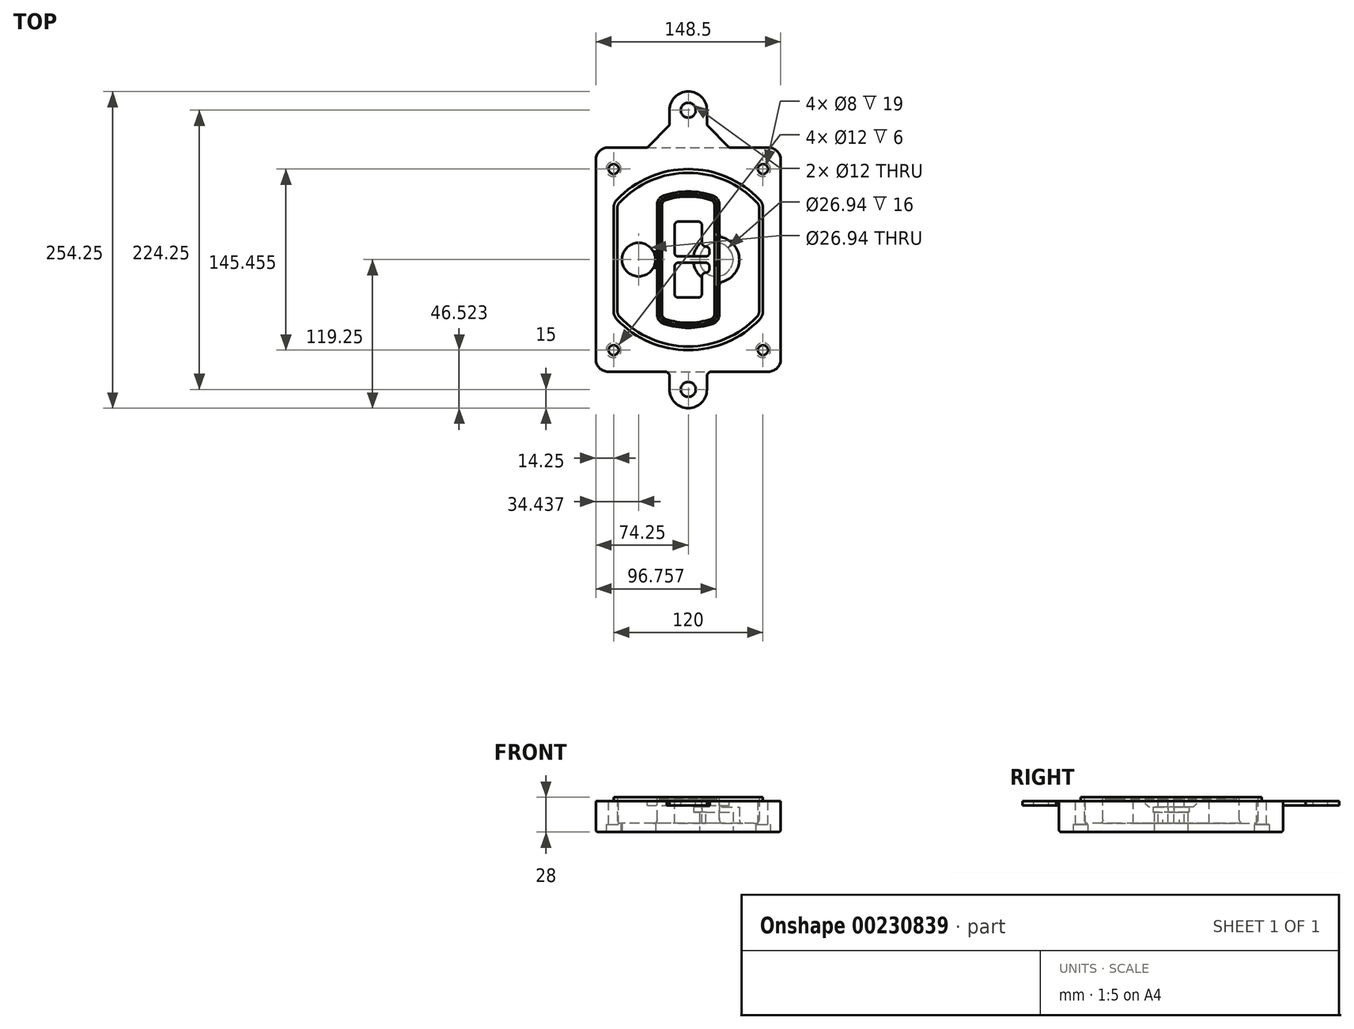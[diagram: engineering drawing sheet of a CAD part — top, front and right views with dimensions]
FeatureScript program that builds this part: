
annotation { "Feature Type Name" : "Feature", "Feature Type Description" : "" }
export const myFeature = defineFeature(function(context is Context, id is Id, definition is map)
    precondition{}
    {
        {
            var Q0;
            Q0=qCreatedBy(makeId("Top.planeOp"),FACE);
            var sketch = newSketch(context, id + "F0", { "sketchPlane" : qUnion([Q0])});
            skPoint(sketch, "E0.rect.middle", {"position": v(0, 0) * mm});
            skLineSegment(sketch, "E1.bottom", {"start": v(-64.25, -90) * mm, "end": v(64.25, -90) * mm});
            skLineSegment(sketch, "E1.top", {"start": v(-64.25, 90) * mm, "end": v(64.25, 90) * mm});
            skLineSegment(sketch, "E1.left", {"start": v(-74.25, -80) * mm, "end": v(-74.25, 80) * mm});
            skLineSegment(sketch, "E1.right", {"start": v(74.25, -80) * mm, "end": v(74.25, 80) * mm});
            skLineSegment(sketch, "E2", {"start": v(-74.25, 90) * mm, "end": v(74.25, -90) * mm, "construction": true});
            skLineSegment(sketch, "E3", {"start": v(74.25, 90) * mm, "end": v(-74.25, -90) * mm, "construction": true});
            skCircle(sketch, "E4", {"center": v(-60, 72.73) * mm, "radius": 4 * mm});
            skCircle(sketch, "E5", {"center": v(60, 72.73) * mm, "radius": 4 * mm});
            skCircle(sketch, "E6", {"center": v(60, -72.73) * mm, "radius": 4 * mm});
            skCircle(sketch, "E7", {"center": v(-60, -72.73) * mm, "radius": 4 * mm});
            skLineSegment(sketch, "E8", {"start": v(-60, 72.73) * mm, "end": v(60, 72.73) * mm, "construction": true});
            skLineSegment(sketch, "E9", {"start": v(60, 72.73) * mm, "end": v(60, -72.73) * mm, "construction": true});
            skLineSegment(sketch, "E10", {"start": v(60, -72.73) * mm, "end": v(-60, -72.73) * mm, "construction": true});
            skLineSegment(sketch, "E11", {"start": v(-60, -72.73) * mm, "end": v(-60, 72.73) * mm, "construction": true});
            skLineSegment(sketch, "E12", {"start": v(-60, 41.18) * mm, "end": v(-60, -41.18) * mm});
            skLineSegment(sketch, "E13", {"start": v(60, 41.18) * mm, "end": v(60, -41.18) * mm});
            skArc(sketch, "E14", {"start": v(57.27, 48.05) * mm, "mid": v(0, 72.73) * mm, "end": v(-57.27, 48.05) * mm});
            skArc(sketch, "E15", {"start": v(-57.27, -48.05) * mm, "mid": v(0, -72.73) * mm, "end": v(57.27, -48.05) * mm});
            skLineSegment(sketch, "E16", {"start": v(-60, 0) * mm, "end": v(60, 0) * mm, "construction": true});
            skPoint(sketch, "E17.visualSharp", {"position": v(-60, -45) * mm});
            skArc(sketch, "E17.filletArc", {"start": v(-60, -41.18) * mm, "mid": v(-59.3, -44.87) * mm, "end": v(-57.27, -48.05) * mm});
            skPoint(sketch, "E18.visualSharp", {"position": v(-60, 45) * mm});
            skArc(sketch, "E18.filletArc", {"start": v(-57.27, 48.05) * mm, "mid": v(-59.3, 44.87) * mm, "end": v(-60, 41.18) * mm});
            skPoint(sketch, "E19.visualSharp", {"position": v(60, 45) * mm});
            skArc(sketch, "E19.filletArc", {"start": v(60, 41.18) * mm, "mid": v(59.3, 44.87) * mm, "end": v(57.27, 48.05) * mm});
            skPoint(sketch, "E20.visualSharp", {"position": v(60, -45) * mm});
            skArc(sketch, "E20.filletArc", {"start": v(57.27, -48.05) * mm, "mid": v(59.3, -44.87) * mm, "end": v(60, -41.18) * mm});
            skPoint(sketch, "E21.visualSharp", {"position": v(-74.25, 90) * mm});
            skArc(sketch, "E21.filletArc", {"start": v(-64.25, 90) * mm, "mid": v(-71.32, 87.07) * mm, "end": v(-74.25, 80) * mm});
            skPoint(sketch, "E22.visualSharp", {"position": v(74.25, 90) * mm});
            skArc(sketch, "E22.filletArc", {"start": v(74.25, 80) * mm, "mid": v(71.32, 87.07) * mm, "end": v(64.25, 90) * mm});
            skPoint(sketch, "E23.visualSharp", {"position": v(74.25, -90) * mm});
            skArc(sketch, "E23.filletArc", {"start": v(64.25, -90) * mm, "mid": v(71.32, -87.07) * mm, "end": v(74.25, -80) * mm});
            skPoint(sketch, "E24.visualSharp", {"position": v(-74.25, -90) * mm});
            skArc(sketch, "E24.filletArc", {"start": v(-74.25, -80) * mm, "mid": v(-71.32, -87.07) * mm, "end": v(-64.25, -90) * mm});
            skArc(sketch, "E25.0", {"start": v(57, 41.18) * mm, "mid": v(56.5, 43.76) * mm, "end": v(55.09, 45.99) * mm});
            skLineSegment(sketch, "E25.1", {"start": v(57, 41.18) * mm, "end": v(57, -41.18) * mm});
            skArc(sketch, "E25.2", {"start": v(55.09, -45.99) * mm, "mid": v(56.5, -43.76) * mm, "end": v(57, -41.18) * mm});
            skArc(sketch, "E25.3", {"start": v(-55.09, -45.99) * mm, "mid": v(0, -69.73) * mm, "end": v(55.09, -45.99) * mm});
            skArc(sketch, "E25.4", {"start": v(-57, -41.18) * mm, "mid": v(-56.5, -43.76) * mm, "end": v(-55.09, -45.99) * mm});
            skArc(sketch, "E25.5", {"start": v(55.09, 45.99) * mm, "mid": v(0, 69.73) * mm, "end": v(-55.09, 45.99) * mm});
            skLineSegment(sketch, "E25.6", {"start": v(-57, 41.18) * mm, "end": v(-57, -41.18) * mm});
            skArc(sketch, "E25.7", {"start": v(-55.09, 45.99) * mm, "mid": v(-56.5, 43.76) * mm, "end": v(-57, 41.18) * mm});
            skArc(sketch, "E26.0", {"start": v(-60.18, 50.8) * mm, "mid": v(-63, 46.35) * mm, "end": v(-64, 41.18) * mm});
            skArc(sketch, "E26.1", {"start": v(60.18, 50.8) * mm, "mid": v(0, 76.73) * mm, "end": v(-60.18, 50.8) * mm});
            skArc(sketch, "E26.2", {"start": v(64, 41.18) * mm, "mid": v(63, 46.35) * mm, "end": v(60.18, 50.8) * mm});
            skLineSegment(sketch, "E26.3", {"start": v(64, 41.18) * mm, "end": v(64, -41.18) * mm});
            skArc(sketch, "E26.4", {"start": v(60.18, -50.8) * mm, "mid": v(63, -46.35) * mm, "end": v(64, -41.18) * mm});
            skLineSegment(sketch, "E26.5", {"start": v(-64, 41.18) * mm, "end": v(-64, -41.18) * mm});
            skArc(sketch, "E26.6", {"start": v(-60.18, -50.8) * mm, "mid": v(0, -76.73) * mm, "end": v(60.18, -50.8) * mm});
            skArc(sketch, "E26.7", {"start": v(-64, -41.18) * mm, "mid": v(-63, -46.35) * mm, "end": v(-60.18, -50.8) * mm});
            skSolve(sketch);
        }
        {
            var Q0;
            Q0=makeQuery(id+"F0.imprint","IMPRINT",FACE,{"disambiguationData":[TD([[makeQuery(id+"F0.imprint","IMPRINT",EDGE,{"derivedFrom":sQuery(id+"F0.wireOp",EDGE,"E1.bottom")}),1.0]])]});
            var Q1;
            Q1=makeQuery(id+"F0.imprint","IMPRINT",FACE,{"disambiguationData":[TD([[makeQuery(id+"F0.imprint","IMPRINT",EDGE,{"derivedFrom":sQuery(id+"F0.wireOp",EDGE,"E12")}),1.0]])]});
            var Q2;
            Q2=makeQuery(id+"F0.imprint","IMPRINT",FACE,{"disambiguationData":[TD([[makeQuery(id+"F0.imprint","IMPRINT",EDGE,{"derivedFrom":sQuery(id+"F0.wireOp",EDGE,"E25.0")}),1.0]])]});
            var Q3;
            Q3=makeQuery(id+"F0.imprint","IMPRINT",FACE,{"disambiguationData":[TD([[makeQuery(id+"F0.imprint","IMPRINT",EDGE,{"derivedFrom":sQuery(id+"F0.wireOp",EDGE,"E12")}),-1.0]])]});
            extrude(context, id + "F1", {"entities" : qUnion([Q0, Q1, Q2, Q3]), "oppositeDirection" : true, "depth" : 25 * mm});
        }
        {
            var Q0;
            Q0=makeQuery(id+"F0.imprint","IMPRINT",FACE,{"disambiguationData":[TD([[makeQuery(id+"F0.imprint","IMPRINT",EDGE,{"derivedFrom":sQuery(id+"F0.wireOp",EDGE,"E12")}),1.0]])]});
            extrude(context, id + "F2", {"entities" : qUnion([Q0]), "operationType" : NewBodyOperationType.ADD, "depth" : 3 * mm});
        }
        {
            var Q0;
            Q0=makeQuery(id+"F0.imprint","IMPRINT",FACE,{"disambiguationData":[TD([[makeQuery(id+"F0.imprint","IMPRINT",EDGE,{"derivedFrom":sQuery(id+"F0.wireOp",EDGE,"E25.0")}),1.0]])]});
            extrude(context, id + "F3", {"entities" : qUnion([Q0]), "operationType" : NewBodyOperationType.REMOVE, "oppositeDirection" : true, "depth" : 18 * mm});
        }
        {
            var Q0;
            Q0=makeQuery(id+"F2.opExtrude","CAP_FACE",FACE,{"disambiguationData":[OSD([sQuery(id+"F0.wireOp",EDGE,"E12"),sQuery(id+"F0.wireOp",EDGE,"E13"),sQuery(id+"F0.wireOp",EDGE,"E14"),sQuery(id+"F0.wireOp",EDGE,"E15"),sQuery(id+"F0.wireOp",EDGE,"E17.filletArc"),sQuery(id+"F0.wireOp",EDGE,"E18.filletArc"),sQuery(id+"F0.wireOp",EDGE,"E19.filletArc"),sQuery(id+"F0.wireOp",EDGE,"E20.filletArc"),sQuery(id+"F0.wireOp",EDGE,"E25.0"),sQuery(id+"F0.wireOp",EDGE,"E25.1"),sQuery(id+"F0.wireOp",EDGE,"E25.2"),sQuery(id+"F0.wireOp",EDGE,"E25.3"),sQuery(id+"F0.wireOp",EDGE,"E25.4"),sQuery(id+"F0.wireOp",EDGE,"E25.5"),sQuery(id+"F0.wireOp",EDGE,"E25.6"),sQuery(id+"F0.wireOp",EDGE,"E25.7")])],"isStart":false});
            var sketch = newSketch(context, id + "F4", { "sketchPlane" : qUnion([Q0])});
            skArc(sketch, "E27.0", {"start": v(-19.58, -51.49) * mm, "mid": v(0, -54.73) * mm, "end": v(19.58, -51.49) * mm});
            skArc(sketch, "E28.0", {"start": v(19.58, 51.49) * mm, "mid": v(0, 54.73) * mm, "end": v(-19.58, 51.49) * mm});
            skLineSegment(sketch, "E29", {"start": v(-25, 43.91) * mm, "end": v(-25, -43.91) * mm});
            skLineSegment(sketch, "E30", {"start": v(25, 43.91) * mm, "end": v(25, -43.91) * mm});
            skLineSegment(sketch, "E31", {"start": v(-25, 49.35) * mm, "end": v(25, 49.35) * mm, "construction": true});
            skLineSegment(sketch, "E32", {"start": v(-25, -49.35) * mm, "end": v(25, -49.35) * mm, "construction": true});
            skPoint(sketch, "E33.visualSharp", {"position": v(-25, 49.35) * mm});
            skArc(sketch, "E33.filletArc", {"start": v(-19.58, 51.49) * mm, "mid": v(-23.5, 48.57) * mm, "end": v(-25, 43.91) * mm});
            skPoint(sketch, "E34.visualSharp", {"position": v(25, 49.35) * mm});
            skArc(sketch, "E34.filletArc", {"start": v(25, 43.91) * mm, "mid": v(23.5, 48.57) * mm, "end": v(19.58, 51.49) * mm});
            skPoint(sketch, "E35.visualSharp", {"position": v(25, -49.35) * mm});
            skArc(sketch, "E35.filletArc", {"start": v(19.58, -51.49) * mm, "mid": v(23.5, -48.57) * mm, "end": v(25, -43.91) * mm});
            skPoint(sketch, "E36.visualSharp", {"position": v(-25, -49.35) * mm});
            skArc(sketch, "E36.filletArc", {"start": v(-25, -43.91) * mm, "mid": v(-23.5, -48.57) * mm, "end": v(-19.58, -51.49) * mm});
            skArc(sketch, "E37.0", {"start": v(55.09, 45.99) * mm, "mid": v(0, 69.73) * mm, "end": v(-55.09, 45.99) * mm});
            skArc(sketch, "E37.1", {"start": v(-55.09, 45.99) * mm, "mid": v(-56.5, 43.76) * mm, "end": v(-57, 41.18) * mm});
            skLineSegment(sketch, "E37.2", {"start": v(-57, 41.18) * mm, "end": v(-57, -41.18) * mm});
            skArc(sketch, "E37.3", {"start": v(-57, -41.18) * mm, "mid": v(-56.5, -43.76) * mm, "end": v(-55.09, -45.99) * mm});
            skArc(sketch, "E37.4", {"start": v(-55.09, -45.99) * mm, "mid": v(0, -69.73) * mm, "end": v(55.09, -45.99) * mm});
            skArc(sketch, "E37.5", {"start": v(55.09, -45.99) * mm, "mid": v(56.5, -43.76) * mm, "end": v(57, -41.18) * mm});
            skLineSegment(sketch, "E37.6", {"start": v(57, 41.18) * mm, "end": v(57, -41.18) * mm});
            skArc(sketch, "E37.7", {"start": v(57, 41.18) * mm, "mid": v(56.5, 43.76) * mm, "end": v(55.09, 45.99) * mm});
            skLineSegment(sketch, "E38.0", {"start": v(23, 43.91) * mm, "end": v(23, -43.91) * mm});
            skArc(sketch, "E38.1", {"start": v(18.93, -49.6) * mm, "mid": v(21.88, -47.4) * mm, "end": v(23, -43.91) * mm});
            skArc(sketch, "E38.2", {"start": v(-18.93, -49.6) * mm, "mid": v(0, -52.73) * mm, "end": v(18.93, -49.6) * mm});
            skArc(sketch, "E38.3", {"start": v(-23, -43.91) * mm, "mid": v(-21.88, -47.4) * mm, "end": v(-18.93, -49.6) * mm});
            skLineSegment(sketch, "E38.4", {"start": v(-23, 43.91) * mm, "end": v(-23, -43.91) * mm});
            skArc(sketch, "E38.5", {"start": v(23, 43.91) * mm, "mid": v(21.88, 47.4) * mm, "end": v(18.93, 49.6) * mm});
            skArc(sketch, "E38.6", {"start": v(-18.93, 49.6) * mm, "mid": v(-21.88, 47.4) * mm, "end": v(-23, 43.91) * mm});
            skArc(sketch, "E38.7", {"start": v(18.93, 49.6) * mm, "mid": v(0, 52.73) * mm, "end": v(-18.93, 49.6) * mm});
            skArc(sketch, "E39.0", {"start": v(21, 43.91) * mm, "mid": v(20.25, 46.24) * mm, "end": v(18.29, 47.7) * mm});
            skLineSegment(sketch, "E39.1", {"start": v(21, 43.91) * mm, "end": v(21, -43.91) * mm});
            skArc(sketch, "E39.2", {"start": v(18.29, -47.7) * mm, "mid": v(20.25, -46.24) * mm, "end": v(21, -43.91) * mm});
            skArc(sketch, "E39.3", {"start": v(-18.29, -47.7) * mm, "mid": v(0, -50.73) * mm, "end": v(18.29, -47.7) * mm});
            skArc(sketch, "E39.4", {"start": v(-21, -43.91) * mm, "mid": v(-20.25, -46.24) * mm, "end": v(-18.29, -47.7) * mm});
            skArc(sketch, "E39.5", {"start": v(18.29, 47.7) * mm, "mid": v(0, 50.73) * mm, "end": v(-18.29, 47.7) * mm});
            skLineSegment(sketch, "E39.6", {"start": v(-21, 43.91) * mm, "end": v(-21, -43.91) * mm});
            skArc(sketch, "E39.7", {"start": v(-18.29, 47.7) * mm, "mid": v(-20.25, 46.24) * mm, "end": v(-21, 43.91) * mm});
            skLineSegment(sketch, "E40", {"start": v(-25, 0) * mm, "end": v(25, 0) * mm, "construction": true});
            skLineSegment(sketch, "E41", {"start": v(-11, 5.5) * mm, "end": v(-11, 27.5) * mm});
            skLineSegment(sketch, "E42", {"start": v(-8, 30.5) * mm, "end": v(8, 30.5) * mm});
            skLineSegment(sketch, "E43", {"start": v(11, 27.5) * mm, "end": v(11, 13.5) * mm});
            skLineSegment(sketch, "E44", {"start": v(14, 10.5) * mm, "end": v(14, 10.5) * mm});
            skLineSegment(sketch, "E45", {"start": v(17, 7.5) * mm, "end": v(17, 5.5) * mm});
            skLineSegment(sketch, "E46", {"start": v(14, 2.5) * mm, "end": v(-8, 2.5) * mm});
            skPoint(sketch, "E47.visualSharp", {"position": v(-11, 30.5) * mm});
            skArc(sketch, "E47.filletArc", {"start": v(-8, 30.5) * mm, "mid": v(-10.12, 29.62) * mm, "end": v(-11, 27.5) * mm});
            skPoint(sketch, "E48.visualSharp", {"position": v(11, 30.5) * mm});
            skArc(sketch, "E48.filletArc", {"start": v(11, 27.5) * mm, "mid": v(10.12, 29.62) * mm, "end": v(8, 30.5) * mm});
            skPoint(sketch, "E49.visualSharp", {"position": v(11, 10.5) * mm});
            skArc(sketch, "E49.filletArc", {"start": v(11, 13.5) * mm, "mid": v(11.88, 11.38) * mm, "end": v(14, 10.5) * mm});
            skPoint(sketch, "E50.visualSharp", {"position": v(17, 10.5) * mm});
            skArc(sketch, "E50.filletArc", {"start": v(17, 7.5) * mm, "mid": v(16.12, 9.62) * mm, "end": v(14, 10.5) * mm});
            skPoint(sketch, "E51.visualSharp", {"position": v(17, 2.5) * mm});
            skArc(sketch, "E51.filletArc", {"start": v(14, 2.5) * mm, "mid": v(16.12, 3.38) * mm, "end": v(17, 5.5) * mm});
            skPoint(sketch, "E52.visualSharp", {"position": v(-11, 2.5) * mm});
            skArc(sketch, "E52.filletArc", {"start": v(-11, 5.5) * mm, "mid": v(-10.12, 3.38) * mm, "end": v(-8, 2.5) * mm});
            skLineSegment(sketch, "E53.0.MirrorCS", {"start": v(14, -2.5) * mm, "end": v(-8, -2.5) * mm});
            skArc(sketch, "E54.0.MirrorCS", {"start": v(-11, -5.5) * mm, "mid": v(-10.12, -3.38) * mm, "end": v(-8, -2.5) * mm});
            skLineSegment(sketch, "E55.0.MirrorCS", {"start": v(-11, -5.5) * mm, "end": v(-11, -27.5) * mm});
            skArc(sketch, "E56.0.MirrorCS", {"start": v(-8, -30.5) * mm, "mid": v(-10.12, -29.62) * mm, "end": v(-11, -27.5) * mm});
            skLineSegment(sketch, "E57.0.MirrorCS", {"start": v(-8, -30.5) * mm, "end": v(8, -30.5) * mm});
            skArc(sketch, "E58.0.MirrorCS", {"start": v(11, -27.5) * mm, "mid": v(10.12, -29.62) * mm, "end": v(8, -30.5) * mm});
            skLineSegment(sketch, "E59.0.MirrorCS", {"start": v(11, -27.5) * mm, "end": v(11, -13.5) * mm});
            skArc(sketch, "E60.0.MirrorCS", {"start": v(11, -13.5) * mm, "mid": v(11.88, -11.38) * mm, "end": v(14, -10.5) * mm});
            skArc(sketch, "E61.0.MirrorCS", {"start": v(17, -7.5) * mm, "mid": v(16.12, -9.62) * mm, "end": v(14, -10.5) * mm});
            skLineSegment(sketch, "E62.0.MirrorCS", {"start": v(17, -7.5) * mm, "end": v(17, -5.5) * mm});
            skArc(sketch, "E63.0.MirrorCS", {"start": v(14, -2.5) * mm, "mid": v(16.12, -3.38) * mm, "end": v(17, -5.5) * mm});
            skSolve(sketch);
        }
        {
            var Q0;
            Q0=makeQuery(id+"F4.imprint","IMPRINT",FACE,{"disambiguationData":[TD([[makeQuery(id+"F4.imprint","IMPRINT",EDGE,{"derivedFrom":sQuery(id+"F4.wireOp",EDGE,"E27.0")}),1.0]])]});
            var Q1;
            Q1=makeQuery(id+"F4.imprint","IMPRINT",FACE,{"disambiguationData":[TD([[makeQuery(id+"F4.imprint","IMPRINT",EDGE,{"derivedFrom":sQuery(id+"F4.wireOp",EDGE,"E38.0")}),-1.0]])]});
            var Q2;
            Q2=makeQuery(id+"F4.imprint","IMPRINT",FACE,{"disambiguationData":[TD([[makeQuery(id+"F4.imprint","IMPRINT",EDGE,{"derivedFrom":sQuery(id+"F4.wireOp",EDGE,"E39.0")}),1.0]])]});
            extrude(context, id + "F5", {"entities" : qUnion([Q0, Q1, Q2]), "operationType" : NewBodyOperationType.ADD, "endBound" : BoundingType.UP_TO_NEXT, "oppositeDirection" : true, "depth" : 25 * mm});
        }
        {
            var Q0;
            Q0=makeQuery(id+"F4.imprint","IMPRINT",FACE,{"disambiguationData":[TD([[makeQuery(id+"F4.imprint","IMPRINT",EDGE,{"derivedFrom":sQuery(id+"F4.wireOp",EDGE,"E38.0")}),-1.0]])]});
            extrude(context, id + "F6", {"entities" : qUnion([Q0]), "operationType" : NewBodyOperationType.REMOVE, "oppositeDirection" : true, "depth" : 2 * mm});
        }
        {
            var Q0;
            Q0=makeQuery(id+"F1.opExtrude","CAP_FACE",FACE,{"disambiguationData":[OSD([sQuery(id+"F0.wireOp",EDGE,"E1.bottom"),sQuery(id+"F0.wireOp",EDGE,"E1.top"),sQuery(id+"F0.wireOp",EDGE,"E1.left"),sQuery(id+"F0.wireOp",EDGE,"E1.right"),sQuery(id+"F0.wireOp",EDGE,"E4"),sQuery(id+"F0.wireOp",EDGE,"E5"),sQuery(id+"F0.wireOp",EDGE,"E6"),sQuery(id+"F0.wireOp",EDGE,"E7"),sQuery(id+"F0.wireOp",EDGE,"E21.filletArc"),sQuery(id+"F0.wireOp",EDGE,"E22.filletArc"),sQuery(id+"F0.wireOp",EDGE,"E23.filletArc"),sQuery(id+"F0.wireOp",EDGE,"E24.filletArc")])],"isStart":false});
            var sketch = newSketch(context, id + "F7", { "sketchPlane" : qUnion([Q0])});
            skCircle(sketch, "E64", {"center": v(22.5, 0) * mm, "radius": 13.47 * mm});
            skCircle(sketch, "E65", {"center": v(-39.81, 0) * mm, "radius": 13.47 * mm});
            skLineSegment(sketch, "E66", {"start": v(74.25, 0) * mm, "end": v(-74.25, 0) * mm});
            skCircle(sketch, "E67", {"center": v(22.5, 0) * mm, "radius": 18.47 * mm});
            skCircle(sketch, "E68", {"center": v(60, -72.73) * mm, "radius": 6 * mm});
            skCircle(sketch, "E69", {"center": v(-60, -72.73) * mm, "radius": 6 * mm});
            skCircle(sketch, "E70", {"center": v(-60, 72.73) * mm, "radius": 6 * mm});
            skCircle(sketch, "E71", {"center": v(60, 72.73) * mm, "radius": 6 * mm});
            skSolve(sketch);
        }
        {
            var Q0;
            {var subQ1=sQuery(id+"F7.wireOp",EDGE,"E66");var subQ4=sQuery(id+"F7.wireOp",EDGE,"E64");var subQ6=makeQuery(id+"F7.imprint","INTERSECT",VERTEX,{"disambiguationData":[OD(0.0)],"derivedFrom":[subQ4,subQ1]});Q0=makeQuery(id+"F7.imprint","IMPRINT",FACE,{"disambiguationData":[TD([[makeQuery(id+"F7.imprint","IMPRINT",EDGE,{"disambiguationData":[TD([[subQ6,-1.0]])],"derivedFrom":subQ4}),-1.0]])]});}
            var Q1;
            {var subQ0=sQuery(id+"F7.wireOp",EDGE,"E66");var subQ1=sQuery(id+"F7.wireOp",EDGE,"E64");var subQ3=makeQuery(id+"F7.imprint","INTERSECT",VERTEX,{"disambiguationData":[OD(0.0)],"derivedFrom":[subQ1,subQ0]});Q1=makeQuery(id+"F7.imprint","IMPRINT",FACE,{"disambiguationData":[TD([[makeQuery(id+"F7.imprint","IMPRINT",EDGE,{"disambiguationData":[TD([[subQ3,-1.0]])],"derivedFrom":subQ1}),1.0]])]});}
            var Q2;
            {var subQ0=sQuery(id+"F7.wireOp",EDGE,"E66");var subQ1=sQuery(id+"F7.wireOp",EDGE,"E64");var subQ3=makeQuery(id+"F7.imprint","INTERSECT",VERTEX,{"disambiguationData":[OD(0.0)],"derivedFrom":[subQ1,subQ0]});Q2=makeQuery(id+"F7.imprint","IMPRINT",FACE,{"disambiguationData":[TD([[makeQuery(id+"F7.imprint","IMPRINT",EDGE,{"disambiguationData":[TD([[subQ3,1.0]])],"derivedFrom":subQ1}),1.0]])]});}
            var Q3;
            {var subQ1=sQuery(id+"F7.wireOp",EDGE,"E66");var subQ4=sQuery(id+"F7.wireOp",EDGE,"E64");var subQ6=makeQuery(id+"F7.imprint","INTERSECT",VERTEX,{"disambiguationData":[OD(0.0)],"derivedFrom":[subQ4,subQ1]});Q3=makeQuery(id+"F7.imprint","IMPRINT",FACE,{"disambiguationData":[TD([[makeQuery(id+"F7.imprint","IMPRINT",EDGE,{"disambiguationData":[TD([[subQ6,1.0]])],"derivedFrom":subQ4}),-1.0]])]});}
            extrude(context, id + "F8", {"entities" : qUnion([Q0, Q1, Q2, Q3]), "operationType" : NewBodyOperationType.ADD, "oppositeDirection" : true, "depth" : 20 * mm});
        }
        {
            var Q0;
            {var subQ0=sQuery(id+"F7.wireOp",EDGE,"E66");var subQ1=sQuery(id+"F7.wireOp",EDGE,"E64");var subQ3=makeQuery(id+"F7.imprint","INTERSECT",VERTEX,{"disambiguationData":[OD(0.0)],"derivedFrom":[subQ1,subQ0]});Q0=makeQuery(id+"F7.imprint","IMPRINT",FACE,{"disambiguationData":[TD([[makeQuery(id+"F7.imprint","IMPRINT",EDGE,{"disambiguationData":[TD([[subQ3,-1.0]])],"derivedFrom":subQ1}),1.0]])]});}
            var Q1;
            {var subQ0=sQuery(id+"F7.wireOp",EDGE,"E66");var subQ1=sQuery(id+"F7.wireOp",EDGE,"E64");var subQ3=makeQuery(id+"F7.imprint","INTERSECT",VERTEX,{"disambiguationData":[OD(0.0)],"derivedFrom":[subQ1,subQ0]});Q1=makeQuery(id+"F7.imprint","IMPRINT",FACE,{"disambiguationData":[TD([[makeQuery(id+"F7.imprint","IMPRINT",EDGE,{"disambiguationData":[TD([[subQ3,1.0]])],"derivedFrom":subQ1}),1.0]])]});}
            extrude(context, id + "F9", {"entities" : qUnion([Q0, Q1]), "operationType" : NewBodyOperationType.REMOVE, "oppositeDirection" : true, "depth" : 16 * mm});
        }
        {
            var Q0;
            {var subQ0=sQuery(id+"F7.wireOp",EDGE,"E66");var subQ1=sQuery(id+"F7.wireOp",EDGE,"E65");var subQ3=makeQuery(id+"F7.imprint","INTERSECT",VERTEX,{"disambiguationData":[OD(0.0)],"derivedFrom":[subQ1,subQ0]});Q0=makeQuery(id+"F7.imprint","IMPRINT",FACE,{"disambiguationData":[TD([[makeQuery(id+"F7.imprint","IMPRINT",EDGE,{"disambiguationData":[TD([[subQ3,-1.0]])],"derivedFrom":subQ1}),1.0]])]});}
            var Q1;
            {var subQ0=sQuery(id+"F7.wireOp",EDGE,"E66");var subQ1=sQuery(id+"F7.wireOp",EDGE,"E65");var subQ3=makeQuery(id+"F7.imprint","INTERSECT",VERTEX,{"disambiguationData":[OD(0.0)],"derivedFrom":[subQ1,subQ0]});Q1=makeQuery(id+"F7.imprint","IMPRINT",FACE,{"disambiguationData":[TD([[makeQuery(id+"F7.imprint","IMPRINT",EDGE,{"disambiguationData":[TD([[subQ3,1.0]])],"derivedFrom":subQ1}),1.0]])]});}
            extrude(context, id + "F10", {"entities" : qUnion([Q0, Q1]), "operationType" : NewBodyOperationType.REMOVE, "oppositeDirection" : true, "depth" : 25 * mm});
        }
        {
            var Q0;
            Q0=makeQuery(id+"F7.imprint","IMPRINT",FACE,{"disambiguationData":[TD([[makeQuery(id+"F7.imprint","IMPRINT",EDGE,{"derivedFrom":sQuery(id+"F7.wireOp",EDGE,"E68")}),1.0]])]});
            var Q1;
            Q1=makeQuery(id+"F7.imprint","IMPRINT",FACE,{"disambiguationData":[TD([[makeQuery(id+"F7.imprint","IMPRINT",EDGE,{"derivedFrom":makeQuery(id+"F1.opExtrude","CAP_EDGE",EDGE,{"disambiguationData":[OSD([sQuery(id+"F0.wireOp",EDGE,"E5")])],"isStart":false})}),-1.0]])]});
            var Q2;
            Q2=makeQuery(id+"F7.imprint","IMPRINT",FACE,{"disambiguationData":[TD([[makeQuery(id+"F7.imprint","IMPRINT",EDGE,{"derivedFrom":sQuery(id+"F7.wireOp",EDGE,"E69")}),1.0]])]});
            var Q3;
            Q3=makeQuery(id+"F7.imprint","IMPRINT",FACE,{"disambiguationData":[TD([[makeQuery(id+"F7.imprint","IMPRINT",EDGE,{"derivedFrom":makeQuery(id+"F1.opExtrude","CAP_EDGE",EDGE,{"disambiguationData":[OSD([sQuery(id+"F0.wireOp",EDGE,"E4")])],"isStart":false})}),-1.0]])]});
            var Q4;
            Q4=makeQuery(id+"F7.imprint","IMPRINT",FACE,{"disambiguationData":[TD([[makeQuery(id+"F7.imprint","IMPRINT",EDGE,{"derivedFrom":sQuery(id+"F7.wireOp",EDGE,"E70")}),1.0]])]});
            var Q5;
            Q5=makeQuery(id+"F7.imprint","IMPRINT",FACE,{"disambiguationData":[TD([[makeQuery(id+"F7.imprint","IMPRINT",EDGE,{"derivedFrom":makeQuery(id+"F1.opExtrude","CAP_EDGE",EDGE,{"disambiguationData":[OSD([sQuery(id+"F0.wireOp",EDGE,"E7")])],"isStart":false})}),-1.0]])]});
            var Q6;
            Q6=makeQuery(id+"F7.imprint","IMPRINT",FACE,{"disambiguationData":[TD([[makeQuery(id+"F7.imprint","IMPRINT",EDGE,{"derivedFrom":sQuery(id+"F7.wireOp",EDGE,"E71")}),1.0]])]});
            var Q7;
            Q7=makeQuery(id+"F7.imprint","IMPRINT",FACE,{"disambiguationData":[TD([[makeQuery(id+"F7.imprint","IMPRINT",EDGE,{"derivedFrom":makeQuery(id+"F1.opExtrude","CAP_EDGE",EDGE,{"disambiguationData":[OSD([sQuery(id+"F0.wireOp",EDGE,"E6")])],"isStart":false})}),-1.0]])]});
            extrude(context, id + "F11", {"entities" : qUnion([Q0, Q1, Q2, Q3, Q4, Q5, Q6, Q7]), "operationType" : NewBodyOperationType.REMOVE, "oppositeDirection" : true, "depth" : 6 * mm});
        }
        {
            var Q0;
            Q0=makeQuery(id+"F9.boolean.opBoolean","COPY",FACE,{"derivedFrom":makeQuery(id+"F9.opExtrude","CAP_FACE",FACE,{"disambiguationData":[OSD([sQuery(id+"F7.wireOp",EDGE,"E64")])],"isStart":false})});
            var sketch = newSketch(context, id + "F12", { "sketchPlane" : qUnion([Q0])});
            skArc(sketch, "E72.0", {"start": v(11, 14.45) * mm, "mid": v(6.45, 9.13) * mm, "end": v(4.2, 2.5) * mm});
            skArc(sketch, "E72.1", {"start": v(4.2, -2.5) * mm, "mid": v(6.45, -9.13) * mm, "end": v(11, -14.45) * mm});
            skLineSegment(sketch, "E73", {"start": v(4.2, -2.5) * mm, "end": v(14, -2.5) * mm});
            skLineSegment(sketch, "E74.0", {"start": v(14, 2.5) * mm, "end": v(4.2, 2.5) * mm});
            skArc(sketch, "E74.1", {"start": v(14, 2.5) * mm, "mid": v(16.12, 3.38) * mm, "end": v(17, 5.5) * mm});
            skLineSegment(sketch, "E74.2", {"start": v(17, 7.5) * mm, "end": v(17, 5.5) * mm});
            skArc(sketch, "E74.3", {"start": v(17, 7.5) * mm, "mid": v(16.12, 9.62) * mm, "end": v(14, 10.5) * mm});
            skArc(sketch, "E74.4", {"start": v(11, 13.5) * mm, "mid": v(11.88, 11.38) * mm, "end": v(14, 10.5) * mm});
            skLineSegment(sketch, "E74.5", {"start": v(11, 14.45) * mm, "end": v(11, 13.5) * mm});
            skLineSegment(sketch, "E74.7", {"start": v(14, -2.5) * mm, "end": v(4.2, -2.5) * mm});
            skArc(sketch, "E74.8", {"start": v(14, -2.5) * mm, "mid": v(16.12, -3.38) * mm, "end": v(17, -5.5) * mm});
            skLineSegment(sketch, "E74.9", {"start": v(17, -7.5) * mm, "end": v(17, -5.5) * mm});
            skArc(sketch, "E74.10", {"start": v(17, -7.5) * mm, "mid": v(16.12, -9.62) * mm, "end": v(14, -10.5) * mm});
            skArc(sketch, "E74.11", {"start": v(11, -13.5) * mm, "mid": v(11.88, -11.38) * mm, "end": v(14, -10.5) * mm});
            skLineSegment(sketch, "E74.12", {"start": v(11, -14.45) * mm, "end": v(11, -13.5) * mm});
            skPoint(sketch, "E75.orphan", {"position": v(11, -27.5) * mm});
            skPoint(sketch, "E76.orphan", {"position": v(-8, -2.5) * mm});
            skPoint(sketch, "E77.orphan", {"position": v(-8, 2.5) * mm});
            skPoint(sketch, "E78.orphan", {"position": v(11, 27.5) * mm});
            skSolve(sketch);
        }
        {
            var Q0;
            {var subQ7=sQuery(id+"F12.wireOp",EDGE,"E72.0");var subQ14=sQuery(id+"F12.wireOp",EDGE,"E72.1");var subQ16=sQuery(id+"F12.wireOp",EDGE,"E74.1");var subQ18=sQuery(id+"F12.wireOp",EDGE,"E74.8");Q0=qUnion([makeQuery(id+"F12.imprint","IMPRINT",FACE,{"disambiguationData":[TD([[makeQuery(id+"F12.imprint","IMPRINT",EDGE,{"derivedFrom":subQ7}),1.0]])]}),makeQuery(id+"F12.imprint","IMPRINT",FACE,{"disambiguationData":[TD([[makeQuery(id+"F12.imprint","IMPRINT",EDGE,{"derivedFrom":subQ14}),1.0]])]}),makeQuery(id+"F12.imprint","IMPRINT",FACE,{"disambiguationData":[TD([[makeQuery(id+"F12.imprint","IMPRINT",EDGE,{"derivedFrom":subQ16}),1.0]])]}),makeQuery(id+"F12.imprint","IMPRINT",FACE,{"disambiguationData":[TD([[makeQuery(id+"F12.imprint","IMPRINT",EDGE,{"derivedFrom":subQ18}),-1.0]])]})]);}
            var Q1;
            Q1=makeQuery(id+"F5.boolean.opBoolean","SPLIT",FACE,{"disambiguationData":[TD([makeQuery(id+"F5.opExtrude","SWEPT_FACE",FACE,{"disambiguationData":[OSD([sQuery(id+"F4.wireOp",EDGE,"E41")])]})])],"derivedFrom":makeQuery(id+"F3.boolean.opBoolean","COPY",FACE,{"derivedFrom":makeQuery(id+"F3.opExtrude","CAP_FACE",FACE,{"disambiguationData":[OSD([sQuery(id+"F0.wireOp",EDGE,"E25.0"),sQuery(id+"F0.wireOp",EDGE,"E25.1"),sQuery(id+"F0.wireOp",EDGE,"E25.2"),sQuery(id+"F0.wireOp",EDGE,"E25.3"),sQuery(id+"F0.wireOp",EDGE,"E25.4"),sQuery(id+"F0.wireOp",EDGE,"E25.5"),sQuery(id+"F0.wireOp",EDGE,"E25.6"),sQuery(id+"F0.wireOp",EDGE,"E25.7")])],"isStart":false})})});
            extrude(context, id + "F13", {"entities" : qUnion([Q0]), "operationType" : NewBodyOperationType.REMOVE, "endBound" : BoundingType.UP_TO_SURFACE, "endBoundEntityFace" : qUnion([Q1]), "depth" : 25 * mm});
        }
        {
            var Q0;
            Q0=makeQuery(id+"F3.boolean.opBoolean","COPY",EDGE,{"derivedFrom":makeQuery(id+"F3.opExtrude","CAP_EDGE",EDGE,{"disambiguationData":[OSD([sQuery(id+"F0.wireOp",EDGE,"E25.6")])],"isStart":false})});
            var Q1;
            Q1=makeQuery(id+"F8.boolean.opBoolean","INTERSECT",EDGE,{"derivedFrom":[makeQuery(id+"F5.opExtrude","SWEPT_FACE",FACE,{"disambiguationData":[OSD([sQuery(id+"F4.wireOp",EDGE,"E30")])]}),makeQuery(id+"F8.opExtrude","CAP_FACE",FACE,{"disambiguationData":[OSD([sQuery(id+"F7.wireOp",EDGE,"E67")])],"isStart":false})]});
            var Q2;
            Q2=makeQuery(id+"F8.boolean.opBoolean","INTERSECT",EDGE,{"disambiguationData":[OD(1.0)],"derivedFrom":[makeQuery(id+"F5.opExtrude","SWEPT_FACE",FACE,{"disambiguationData":[OSD([sQuery(id+"F4.wireOp",EDGE,"E30")])]}),makeQuery(id+"F8.opExtrude","SWEPT_FACE",FACE,{"disambiguationData":[OSD([sQuery(id+"F7.wireOp",EDGE,"E67")])]})]});
            var Q3;
            {var subQ0=sQuery(id+"F4.wireOp",EDGE,"E30");Q3=makeQuery(id+"F8.boolean.opBoolean","SPLIT",EDGE,{"disambiguationData":[TD([makeQuery(id+"F5.opExtrude","SWEPT_FACE",FACE,{"disambiguationData":[OSD([sQuery(id+"F4.wireOp",EDGE,"E35.filletArc")])]})])],"derivedFrom":makeQuery(id+"F5.opExtrude","CAP_EDGE",EDGE,{"disambiguationData":[OSD([subQ0])],"isStart":false})});}
            var Q4;
            {var subQ0=sQuery(id+"F0.wireOp",EDGE,"E25.7");var subQ1=sQuery(id+"F0.wireOp",EDGE,"E25.1");var subQ2=sQuery(id+"F0.wireOp",EDGE,"E25.6");var subQ3=sQuery(id+"F0.wireOp",EDGE,"E25.5");var subQ4=sQuery(id+"F0.wireOp",EDGE,"E25.4");var subQ5=sQuery(id+"F0.wireOp",EDGE,"E25.0");var subQ6=sQuery(id+"F0.wireOp",EDGE,"E25.2");var subQ7=sQuery(id+"F0.wireOp",EDGE,"E25.3");Q4=makeQuery(id+"F8.boolean.opBoolean","INTERSECT",EDGE,{"derivedFrom":[makeQuery(id+"F5.boolean.opBoolean","SPLIT",FACE,{"disambiguationData":[TD([makeQuery(id+"F2.opExtrude","SWEPT_FACE",FACE,{"disambiguationData":[OSD([subQ5])]})])],"derivedFrom":makeQuery(id+"F3.boolean.opBoolean","COPY",FACE,{"derivedFrom":makeQuery(id+"F3.opExtrude","CAP_FACE",FACE,{"disambiguationData":[OSD([subQ5,subQ1,subQ6,subQ7,subQ4,subQ3,subQ2,subQ0])],"isStart":false})})}),makeQuery(id+"F8.opExtrude","SWEPT_FACE",FACE,{"disambiguationData":[OSD([sQuery(id+"F7.wireOp",EDGE,"E67")])]})]});}
            var Q5;
            Q5=makeQuery(id+"F8.boolean.opBoolean","INTERSECT",EDGE,{"disambiguationData":[OD(0.0)],"derivedFrom":[makeQuery(id+"F5.opExtrude","SWEPT_FACE",FACE,{"disambiguationData":[OSD([sQuery(id+"F4.wireOp",EDGE,"E30")])]}),makeQuery(id+"F8.opExtrude","SWEPT_FACE",FACE,{"disambiguationData":[OSD([sQuery(id+"F7.wireOp",EDGE,"E67")])]})]});
            fillet(context, id + "F14", {"entities" : qUnion([Q0, Q1, Q2, Q3, Q4, Q5]), "radius" : 3 * mm, "tangentPropagation" : true, "allowEdgeOverflow" : false});
        }
        {
            var Q0;
            Q0=makeQuery(id+"F1.opExtrude","CAP_EDGE",EDGE,{"disambiguationData":[OSD([sQuery(id+"F0.wireOp",EDGE,"E1.bottom")])],"isStart":false});
            fillet(context, id + "F15", {"entities" : qUnion([Q0]), "radius" : 2 * mm, "tangentPropagation" : true, "allowEdgeOverflow" : false});
        }
        {
            var Q0;
            {var subQ0=sQuery(id+"F0.wireOp",EDGE,"E22.filletArc");var subQ1=sQuery(id+"F0.wireOp",EDGE,"E7");var subQ2=sQuery(id+"F0.wireOp",EDGE,"E6");var subQ3=sQuery(id+"F0.wireOp",EDGE,"E5");var subQ4=sQuery(id+"F0.wireOp",EDGE,"E4");var subQ5=sQuery(id+"F0.wireOp",EDGE,"E1.bottom");var subQ6=sQuery(id+"F0.wireOp",EDGE,"E21.filletArc");var subQ7=sQuery(id+"F0.wireOp",EDGE,"E1.top");var subQ8=sQuery(id+"F0.wireOp",EDGE,"E1.left");var subQ9=sQuery(id+"F0.wireOp",EDGE,"E1.right");var subQ10=sQuery(id+"F0.wireOp",EDGE,"E23.filletArc");var subQ11=sQuery(id+"F0.wireOp",EDGE,"E24.filletArc");Q0=makeQuery(id+"F2.boolean.opBoolean","SPLIT",FACE,{"disambiguationData":[TD([makeQuery(id+"F1.opExtrude","SWEPT_FACE",FACE,{"disambiguationData":[OSD([subQ5])]})])],"derivedFrom":makeQuery(id+"F1.opExtrude","CAP_FACE",FACE,{"disambiguationData":[OSD([subQ5,subQ7,subQ8,subQ9,subQ4,subQ3,subQ2,subQ1,subQ6,subQ0,subQ10,subQ11])],"isStart":true})});}
            var sketch = newSketch(context, id + "F16", { "sketchPlane" : qUnion([Q0])});
            skCircle(sketch, "E79", {"center": v(0, 120) * mm, "radius": 6 * mm});
            skArc(sketch, "E80", {"start": v(15, 120) * mm, "mid": v(0, 135) * mm, "end": v(-15, 120) * mm});
            skLineSegment(sketch, "E81", {"start": v(-15, 120) * mm, "end": v(-15, 108) * mm});
            skLineSegment(sketch, "E82", {"start": v(15, 120) * mm, "end": v(15, 108) * mm});
            skLineSegment(sketch, "E83", {"start": v(-33, 90) * mm, "end": v(-15, 108) * mm});
            skLineSegment(sketch, "E84", {"start": v(15, 108) * mm, "end": v(33, 90) * mm});
            skArc(sketch, "E85.MirrorC", {"start": v(15, -104.25) * mm, "mid": v(0, -119.25) * mm, "end": v(-15, -104.25) * mm});
            skCircle(sketch, "E86.MirrorC", {"center": v(0, -104.25) * mm, "radius": 6 * mm});
            skLineSegment(sketch, "E87.MirrorCS", {"start": v(-33, -74.25) * mm, "end": v(-15, -92.25) * mm});
            skLineSegment(sketch, "E88.MirrorCS", {"start": v(15, -92.25) * mm, "end": v(33, -74.25) * mm});
            skLineSegment(sketch, "E89.MirrorCS", {"start": v(15, -104.25) * mm, "end": v(15, -92.25) * mm});
            skLineSegment(sketch, "E90.MirrorCS", {"start": v(-15, -104.25) * mm, "end": v(-15, -92.25) * mm});
            skPoint(sketch, "E91.orphan", {"position": v(0, 90) * mm});
            skPoint(sketch, "E92.orphan", {"position": v(-15, 90) * mm});
            skSolve(sketch);
        }
        {
            var Q0;
            {var subQ1=sQuery(id+"F16.wireOp",EDGE,"E88.MirrorCS");Q0=makeQuery(id+"F16.imprint","IMPRINT",FACE,{"disambiguationData":[TD([[makeQuery(id+"F16.imprint","IMPRINT",EDGE,{"derivedFrom":subQ1}),1.0]])]});}
            var Q1;
            Q1=makeQuery(id+"F16.imprint","IMPRINT",FACE,{"disambiguationData":[TD([[makeQuery(id+"F16.imprint","IMPRINT",EDGE,{"derivedFrom":sQuery(id+"F16.wireOp",EDGE,"E79")}),-1.0]])]});
            extrude(context, id + "F17", {"entities" : qUnion([Q0, Q1]), "operationType" : NewBodyOperationType.ADD, "oppositeDirection" : true, "depth" : 3.7 * mm});
        }
    });
